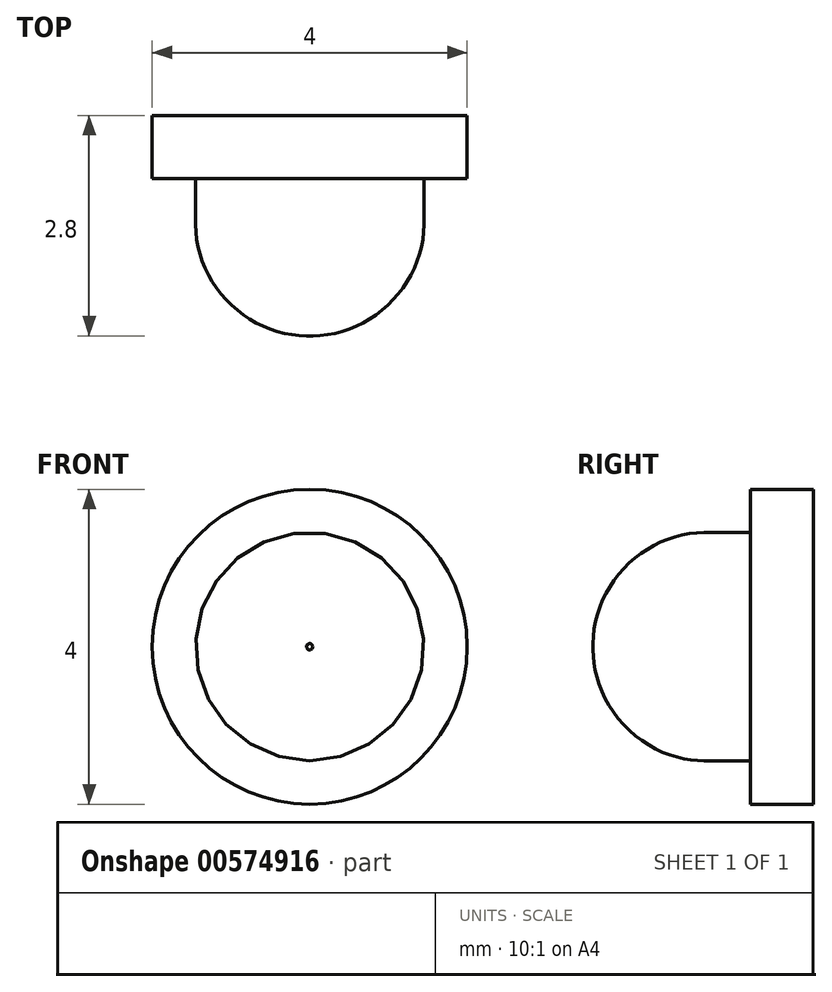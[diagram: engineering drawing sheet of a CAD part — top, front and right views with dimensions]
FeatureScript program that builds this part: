
annotation { "Feature Type Name" : "Feature", "Feature Type Description" : "" }
export const myFeature = defineFeature(function(context is Context, id is Id, definition is map)
    precondition{}
    {
        {
            var Q0;
            Q0=qCreatedBy(makeId("Front.planeOp"),FACE);
            var sketch = newSketch(context, id + "F0", { "sketchPlane" : qUnion([Q0])});
            skCircle(sketch, "E0", {"center": v(0, 0) * mm, "radius": 2 * mm});
            skSolve(sketch);
        }
        {
            var Q0;
            Q0=makeQuery(id+"F0.imprint","IMPRINT",FACE,{"disambiguationData":[TD([[makeQuery(id+"F0.imprint","IMPRINT",EDGE,{"derivedFrom":sQuery(id+"F0.wireOp",EDGE,"E0")}),1.0]])]});
            extrude(context, id + "F1", {"entities" : qUnion([Q0]), "depth" : 0.8 * mm, "offsetDistance" : 25 * mm});
        }
        {
            var Q0;
            Q0=makeQuery(id+"F1.opExtrude","CAP_FACE",FACE,{"disambiguationData":[OSD([sQuery(id+"F0.wireOp",EDGE,"E0")])],"isStart":false});
            var sketch = newSketch(context, id + "F2", { "sketchPlane" : qUnion([Q0])});
            skCircle(sketch, "E1", {"center": v(0, 0) * mm, "radius": 1.45 * mm});
            skSolve(sketch);
        }
        {
            var Q0;
            Q0=makeQuery(id+"F2.imprint","IMPRINT",FACE,{"disambiguationData":[TD([[makeQuery(id+"F2.imprint","IMPRINT",EDGE,{"derivedFrom":sQuery(id+"F2.wireOp",EDGE,"E1")}),1.0]])]});
            extrude(context, id + "F3", {"entities" : qUnion([Q0]), "depth" : 2 * mm, "offsetDistance" : 25 * mm});
        }
        {
            var Q0;
            Q0=makeQuery(id+"F3.opExtrude","CAP_EDGE",EDGE,{"disambiguationData":[OSD([sQuery(id+"F2.wireOp",EDGE,"E1")])],"isStart":false});
            fillet(context, id + "F4", {"entities" : qUnion([Q0]), "radius" : 1.41 * mm, "tangentPropagation" : true, "rho" : 0.4, "crossSection" : FilletCrossSection.CONIC, "allowEdgeOverflow" : false});
        }
    });
